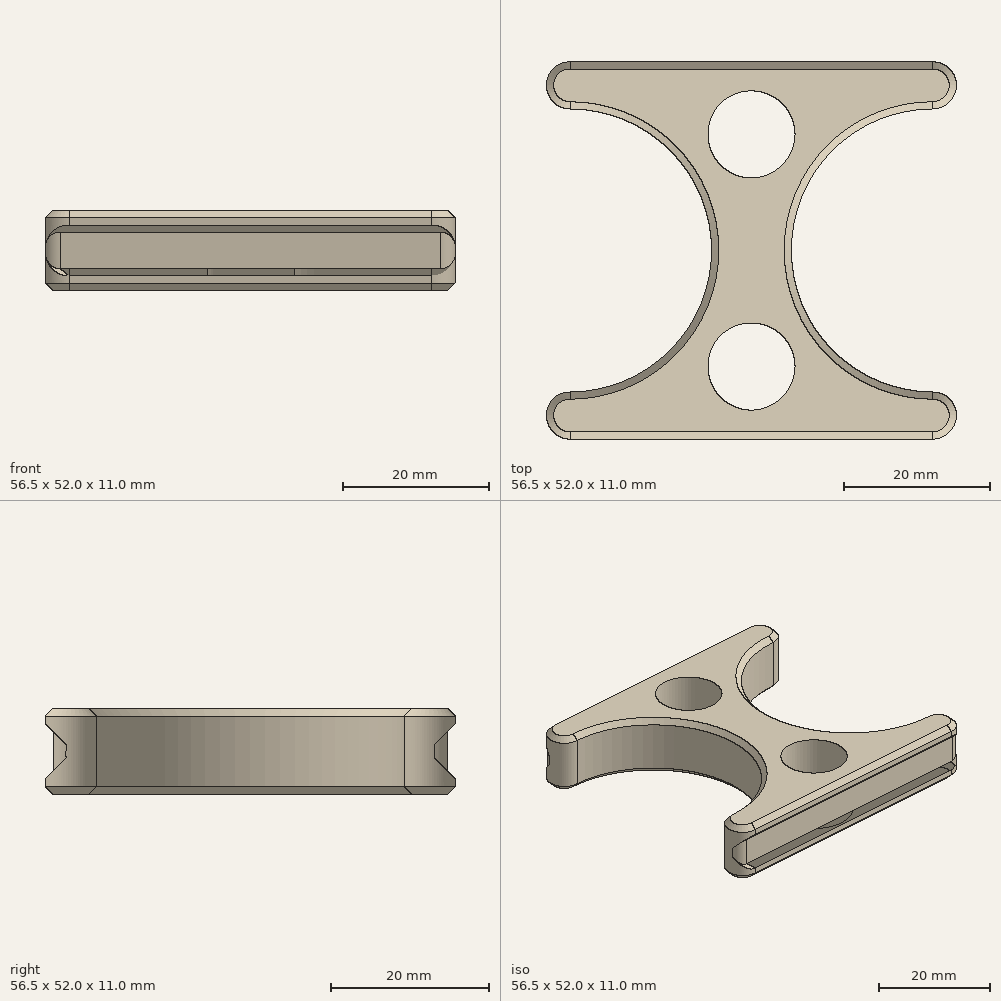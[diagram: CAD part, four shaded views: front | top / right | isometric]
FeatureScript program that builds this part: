
annotation { "Feature Type Name" : "Feature", "Feature Type Description" : "" }
export const myFeature = defineFeature(function(context is Context, id is Id, definition is map)
    precondition{}
    {
        {
            var Q0;
            Q0=qCreatedBy(makeId("Top.planeOp"),FACE);
            var sketch = newSketch(context, id + "F0", { "sketchPlane" : qUnion([Q0])});
            skLineSegment(sketch, "E0.rect.bottom", {"start": v(25, 26) * mm, "end": v(-25, 26) * mm, "construction": true});
            skLineSegment(sketch, "E0.rect.top", {"start": v(25, -26) * mm, "end": v(-25, -26) * mm, "construction": true});
            skLineSegment(sketch, "E0.rect.left", {"start": v(25, 26) * mm, "end": v(25, -26) * mm, "construction": true});
            skLineSegment(sketch, "E0.rect.right", {"start": v(-25, 26) * mm, "end": v(-25, -26) * mm, "construction": true});
            skPoint(sketch, "E0.rect.middle", {"position": v(0, 0) * mm});
            skLineSegment(sketch, "E1.rect.bottom", {"start": v(25, 19.5) * mm, "end": v(-25, 19.5) * mm, "construction": true});
            skLineSegment(sketch, "E1.rect.top", {"start": v(25, -19.5) * mm, "end": v(-25, -19.5) * mm, "construction": true});
            skLineSegment(sketch, "E1.rect.left", {"start": v(25, 19.5) * mm, "end": v(25, -19.5) * mm, "construction": true});
            skLineSegment(sketch, "E1.rect.right", {"start": v(-25, 19.5) * mm, "end": v(-25, -19.5) * mm, "construction": true});
            skArc(sketch, "E2", {"start": v(-25, -19.5) * mm, "mid": v(-5.5, 0) * mm, "end": v(-25, 19.5) * mm});
            skArc(sketch, "E3", {"start": v(25, 19.5) * mm, "mid": v(5.5, 0) * mm, "end": v(25, -19.5) * mm});
            skLineSegment(sketch, "E4", {"start": v(-25, -26) * mm, "end": v(25, -26) * mm});
            skLineSegment(sketch, "E5", {"start": v(-25, 26) * mm, "end": v(25, 26) * mm});
            skLineSegment(sketch, "E6", {"start": v(-25, 26) * mm, "end": v(-25, 19.5) * mm, "construction": true});
            skLineSegment(sketch, "E7", {"start": v(25, 26) * mm, "end": v(25, 19.5) * mm, "construction": true});
            skLineSegment(sketch, "E8", {"start": v(25, -19.5) * mm, "end": v(25, -26) * mm, "construction": true});
            skLineSegment(sketch, "E9", {"start": v(-25, -19.5) * mm, "end": v(-25, -26) * mm, "construction": true});
            skArc(sketch, "E10", {"start": v(-25, 26) * mm, "mid": v(-28.25, 22.75) * mm, "end": v(-25, 19.5) * mm});
            skArc(sketch, "E11", {"start": v(25, 19.5) * mm, "mid": v(28.25, 22.75) * mm, "end": v(25, 26) * mm});
            skArc(sketch, "E12", {"start": v(25, -26) * mm, "mid": v(28.25, -22.75) * mm, "end": v(25, -19.5) * mm});
            skArc(sketch, "E13", {"start": v(-25, -19.5) * mm, "mid": v(-28.25, -22.75) * mm, "end": v(-25, -26) * mm});
            skArc(sketch, "E14.0", {"start": v(-25, -21.5) * mm, "mid": v(-26.25, -22.75) * mm, "end": v(-25, -24) * mm});
            skLineSegment(sketch, "E14.1", {"start": v(-25, -24) * mm, "end": v(25, -24) * mm});
            skArc(sketch, "E14.2", {"start": v(-25, -21.5) * mm, "mid": v(-3.5, 0) * mm, "end": v(-25, 21.5) * mm});
            skArc(sketch, "E14.3", {"start": v(25, -24) * mm, "mid": v(26.25, -22.75) * mm, "end": v(25, -21.5) * mm});
            skArc(sketch, "E14.4", {"start": v(-25, 24) * mm, "mid": v(-26.25, 22.75) * mm, "end": v(-25, 21.5) * mm});
            skLineSegment(sketch, "E14.5", {"start": v(-25, 24) * mm, "end": v(25, 24) * mm});
            skArc(sketch, "E14.6", {"start": v(25, 21.5) * mm, "mid": v(26.25, 22.75) * mm, "end": v(25, 24) * mm});
            skArc(sketch, "E14.7", {"start": v(25, 21.5) * mm, "mid": v(3.5, 0) * mm, "end": v(25, -21.5) * mm});
            skSolve(sketch);
        }
        {
            var Q0;
            Q0=makeQuery(id+"F0.imprint","IMPRINT",FACE,{"disambiguationData":[TD([[makeQuery(id+"F0.imprint","IMPRINT",EDGE,{"derivedFrom":sQuery(id+"F0.wireOp",EDGE,"E2")}),-1.0]])]});
            var Q1;
            Q1=makeQuery(id+"F0.imprint","IMPRINT",FACE,{"disambiguationData":[TD([[makeQuery(id+"F0.imprint","IMPRINT",EDGE,{"derivedFrom":sQuery(id+"F0.wireOp",EDGE,"E14.0")}),1.0]])]});
            extrude(context, id + "F1", {"entities" : qUnion([Q0, Q1]), "depth" : 11 * mm});
        }
        {
            var Q0;
            Q0=makeQuery(id+"F1.opExtrude","SWEPT_FACE",FACE,{"disambiguationData":[OSD([sQuery(id+"F0.wireOp",EDGE,"E4")])]});
            var sketch = newSketch(context, id + "F2", { "sketchPlane" : qUnion([Q0])});
            skLineSegment(sketch, "E15", {"start": v(0, 11) * mm, "end": v(0, 0) * mm, "construction": true});
            skLineSegment(sketch, "E16.rect.bottom", {"start": v(34.25, 9) * mm, "end": v(-34.25, 9) * mm});
            skLineSegment(sketch, "E16.rect.top", {"start": v(34.25, 2) * mm, "end": v(-34.25, 2) * mm});
            skLineSegment(sketch, "E16.rect.left", {"start": v(34.25, 9) * mm, "end": v(34.25, 2) * mm});
            skLineSegment(sketch, "E16.rect.right", {"start": v(-34.25, 9) * mm, "end": v(-34.25, 2) * mm});
            skPoint(sketch, "E16.rect.middle", {"position": v(0, 5.5) * mm});
            skSolve(sketch);
        }
        {
            var Q0;
            {var subQ0=sQuery(id+"F2.wireOp",EDGE,"E16.rect.right");Q0=makeQuery(id+"F2.imprint","IMPRINT",FACE,{"disambiguationData":[TD([[makeQuery(id+"F2.imprint","IMPRINT",EDGE,{"derivedFrom":subQ0}),1.0]])]});}
            var Q1;
            {var subQ0=sQuery(id+"F2.wireOp",EDGE,"E16.rect.bottom");var subQ1=sQuery(id+"F0.wireOp",EDGE,"E4");var subQ2=makeQuery(id+"F1.opExtrude","SWEPT_EDGE",EDGE,{"disambiguationData":[OSD([subQ1,sQuery(id+"F0.wireOp",EDGE,"E12")])]});var subQ3=makeQuery(id+"F2.imprint","INTERSECT",VERTEX,{"derivedFrom":[subQ2,subQ0]});Q1=makeQuery(id+"F2.imprint","IMPRINT",FACE,{"disambiguationData":[TD([[makeQuery(id+"F2.imprint","IMPRINT",EDGE,{"disambiguationData":[TD([[subQ3,-1.0]])],"derivedFrom":subQ0}),1.0]])]});}
            var Q2;
            {var subQ0=sQuery(id+"F2.wireOp",EDGE,"E16.rect.left");Q2=makeQuery(id+"F2.imprint","IMPRINT",FACE,{"disambiguationData":[TD([[makeQuery(id+"F2.imprint","IMPRINT",EDGE,{"derivedFrom":subQ0}),-1.0]])]});}
            extrude(context, id + "F3", {"entities" : qUnion([Q0, Q1, Q2]), "oppositeDirection" : true, "depth" : 1 * mm});
        }
        {
            var Q0;
            Q0=makeQuery(id+"F3.opExtrude","SWEPT_BODY",BODY,{"disambiguationData":[OSD([sQuery(id+"F2.wireOp",EDGE,"E16.rect.bottom"),sQuery(id+"F2.wireOp",EDGE,"E16.rect.top"),sQuery(id+"F2.wireOp",EDGE,"E16.rect.left"),sQuery(id+"F2.wireOp",EDGE,"E16.rect.right")])]});
            transform(context, id + "F4", {"entities" : qUnion([Q0]), "transformType" : TransformType.TRANSLATION_3D, "dx" : 0 * mm, "dy" : 51 * mm, "dz" : 0 * mm, "makeCopy" : true});
        }
        {
            var Q0;
            Q0=makeQuery(id+"F4.opPattern","COPY",BODY,{"derivedFrom":makeQuery(id+"F3.opExtrude","SWEPT_BODY",BODY,{"disambiguationData":[OSD([sQuery(id+"F2.wireOp",EDGE,"E16.rect.bottom"),sQuery(id+"F2.wireOp",EDGE,"E16.rect.top"),sQuery(id+"F2.wireOp",EDGE,"E16.rect.left"),sQuery(id+"F2.wireOp",EDGE,"E16.rect.right")])]}),"instanceName":"1"});
            var Q1;
            Q1=makeQuery(id+"F3.opExtrude","SWEPT_BODY",BODY,{"disambiguationData":[OSD([sQuery(id+"F2.wireOp",EDGE,"E16.rect.bottom"),sQuery(id+"F2.wireOp",EDGE,"E16.rect.top"),sQuery(id+"F2.wireOp",EDGE,"E16.rect.left"),sQuery(id+"F2.wireOp",EDGE,"E16.rect.right")])]});
            var Q2;
            Q2=makeQuery(id+"F1.opExtrude","SWEPT_BODY",BODY,{"disambiguationData":[OSD([sQuery(id+"F0.wireOp",EDGE,"E2"),sQuery(id+"F0.wireOp",EDGE,"E3"),sQuery(id+"F0.wireOp",EDGE,"E4"),sQuery(id+"F0.wireOp",EDGE,"E5"),sQuery(id+"F0.wireOp",EDGE,"E10"),sQuery(id+"F0.wireOp",EDGE,"E11"),sQuery(id+"F0.wireOp",EDGE,"E12"),sQuery(id+"F0.wireOp",EDGE,"E13")])]});
            booleanBodies(context, id + "F5", {"operationType" : BooleanOperationType.SUBTRACTION, "tools" : qUnion([Q0, Q1]), "targets" : qUnion([Q2])});
        }
        {
            var Q0;
            Q0=makeQuery(id+"F1.opExtrude","CAP_EDGE",EDGE,{"disambiguationData":[OSD([sQuery(id+"F0.wireOp",EDGE,"E2")])],"isStart":false});
            var Q1;
            Q1=makeQuery(id+"F1.opExtrude","CAP_EDGE",EDGE,{"disambiguationData":[OSD([sQuery(id+"F0.wireOp",EDGE,"E2")])],"isStart":true});
            chamfer(context, id + "F6", {"entities" : qUnion([Q0, Q1]), "width" : 1 * mm, "tangentPropagation" : true});
        }
        {
            var Q0;
            Q0=makeQuery(id+"F5.opBoolean","COPY",EDGE,{"derivedFrom":makeQuery(id+"F3.opExtrude","CAP_EDGE",EDGE,{"disambiguationData":[OSD([sQuery(id+"F2.wireOp",EDGE,"E16.rect.bottom")])],"isStart":false})});
            var Q1;
            Q1=makeQuery(id+"F5.opBoolean","COPY",EDGE,{"derivedFrom":makeQuery(id+"F3.opExtrude","CAP_EDGE",EDGE,{"disambiguationData":[OSD([sQuery(id+"F2.wireOp",EDGE,"E16.rect.top")])],"isStart":false})});
            var Q2;
            Q2=makeQuery(id+"F5.opBoolean","COPY",EDGE,{"derivedFrom":makeQuery(id+"F4.opPattern","COPY",EDGE,{"derivedFrom":makeQuery(id+"F3.opExtrude","CAP_EDGE",EDGE,{"disambiguationData":[OSD([sQuery(id+"F2.wireOp",EDGE,"E16.rect.bottom")])],"isStart":true}),"instanceName":"1"})});
            var Q3;
            Q3=makeQuery(id+"F5.opBoolean","COPY",EDGE,{"derivedFrom":makeQuery(id+"F4.opPattern","COPY",EDGE,{"derivedFrom":makeQuery(id+"F3.opExtrude","CAP_EDGE",EDGE,{"disambiguationData":[OSD([sQuery(id+"F2.wireOp",EDGE,"E16.rect.top")])],"isStart":true}),"instanceName":"1"})});
            chamfer(context, id + "F7", {"entities" : qUnion([Q0, Q1, Q2, Q3]), "width" : 1 * mm});
        }
        {
            var Q0;
            Q0=makeQuery(id+"F5.opBoolean","INTERSECT",EDGE,{"derivedFrom":[makeQuery(id+"F1.opExtrude","SWEPT_FACE",FACE,{"disambiguationData":[OSD([sQuery(id+"F0.wireOp",EDGE,"E11")])]}),makeQuery(id+"F4.opPattern","COPY",FACE,{"derivedFrom":makeQuery(id+"F3.opExtrude","CAP_FACE",FACE,{"disambiguationData":[OSD([sQuery(id+"F2.wireOp",EDGE,"E16.rect.bottom"),sQuery(id+"F2.wireOp",EDGE,"E16.rect.top"),sQuery(id+"F2.wireOp",EDGE,"E16.rect.left"),sQuery(id+"F2.wireOp",EDGE,"E16.rect.right")])],"isStart":true}),"instanceName":"1"})]});
            var Q1;
            Q1=makeQuery(id+"F5.opBoolean","INTERSECT",EDGE,{"derivedFrom":[makeQuery(id+"F1.opExtrude","SWEPT_FACE",FACE,{"disambiguationData":[OSD([sQuery(id+"F0.wireOp",EDGE,"E10")])]}),makeQuery(id+"F4.opPattern","COPY",FACE,{"derivedFrom":makeQuery(id+"F3.opExtrude","CAP_FACE",FACE,{"disambiguationData":[OSD([sQuery(id+"F2.wireOp",EDGE,"E16.rect.bottom"),sQuery(id+"F2.wireOp",EDGE,"E16.rect.top"),sQuery(id+"F2.wireOp",EDGE,"E16.rect.left"),sQuery(id+"F2.wireOp",EDGE,"E16.rect.right")])],"isStart":true}),"instanceName":"1"})]});
            var Q2;
            Q2=makeQuery(id+"F5.opBoolean","INTERSECT",EDGE,{"derivedFrom":[makeQuery(id+"F1.opExtrude","SWEPT_FACE",FACE,{"disambiguationData":[OSD([sQuery(id+"F0.wireOp",EDGE,"E13")])]}),makeQuery(id+"F3.opExtrude","CAP_FACE",FACE,{"disambiguationData":[OSD([sQuery(id+"F2.wireOp",EDGE,"E16.rect.bottom"),sQuery(id+"F2.wireOp",EDGE,"E16.rect.top"),sQuery(id+"F2.wireOp",EDGE,"E16.rect.left"),sQuery(id+"F2.wireOp",EDGE,"E16.rect.right")])],"isStart":false})]});
            var Q3;
            Q3=makeQuery(id+"F5.opBoolean","INTERSECT",EDGE,{"derivedFrom":[makeQuery(id+"F1.opExtrude","SWEPT_FACE",FACE,{"disambiguationData":[OSD([sQuery(id+"F0.wireOp",EDGE,"E12")])]}),makeQuery(id+"F3.opExtrude","CAP_FACE",FACE,{"disambiguationData":[OSD([sQuery(id+"F2.wireOp",EDGE,"E16.rect.bottom"),sQuery(id+"F2.wireOp",EDGE,"E16.rect.top"),sQuery(id+"F2.wireOp",EDGE,"E16.rect.left"),sQuery(id+"F2.wireOp",EDGE,"E16.rect.right")])],"isStart":false})]});
            fillet(context, id + "F8", {"entities" : qUnion([Q0, Q1, Q2, Q3]), "radius" : 2 * mm, "allowEdgeOverflow" : false});
        }
        {
            var Q0;
            Q0=makeQuery(id+"F1.opExtrude","CAP_FACE",FACE,{"disambiguationData":[OSD([sQuery(id+"F0.wireOp",EDGE,"E2"),sQuery(id+"F0.wireOp",EDGE,"E3"),sQuery(id+"F0.wireOp",EDGE,"E4"),sQuery(id+"F0.wireOp",EDGE,"E5"),sQuery(id+"F0.wireOp",EDGE,"E10"),sQuery(id+"F0.wireOp",EDGE,"E11"),sQuery(id+"F0.wireOp",EDGE,"E12"),sQuery(id+"F0.wireOp",EDGE,"E13")])],"isStart":false});
            var sketch = newSketch(context, id + "F9", { "sketchPlane" : qUnion([Q0])});
            skCircle(sketch, "E17", {"center": v(0, -16) * mm, "radius": 6 * mm});
            skPoint(sketch, "E17.centerSnap0", {"position": v(0, -25) * mm});
            skCircle(sketch, "E18.MirrorC", {"center": v(0, 16) * mm, "radius": 6 * mm});
            skSolve(sketch);
        }
        {
            var Q0;
            Q0 = qSketchRegion(id + "F9", true);
            extrude(context, id + "F10", {"entities" : qUnion([Q0]), "operationType" : NewBodyOperationType.REMOVE, "endBound" : BoundingType.THROUGH_ALL, "oppositeDirection" : true, "depth" : 25 * mm});
        }
        {
            var Q0;
            Q0=makeQuery(id+"F10.boolean.opBoolean","COPY",EDGE,{"derivedFrom":makeQuery(id+"F10.opExtrude","CAP_EDGE",EDGE,{"disambiguationData":[OSD([sQuery(id+"F9.wireOp",EDGE,"E18.MirrorC")])],"isStart":true})});
            var Q1;
            Q1=makeQuery(id+"F10.boolean.opBoolean","COPY",EDGE,{"derivedFrom":makeQuery(id+"F10.opExtrude","CAP_EDGE",EDGE,{"disambiguationData":[OSD([sQuery(id+"F9.wireOp",EDGE,"E17")])],"isStart":true})});
            var Q2;
            Q2=makeQuery(id+"F10.boolean.opBoolean","INTERSECT",EDGE,{"derivedFrom":[makeQuery(id+"F1.opExtrude","CAP_FACE",FACE,{"disambiguationData":[OSD([sQuery(id+"F0.wireOp",EDGE,"E2"),sQuery(id+"F0.wireOp",EDGE,"E3"),sQuery(id+"F0.wireOp",EDGE,"E4"),sQuery(id+"F0.wireOp",EDGE,"E5"),sQuery(id+"F0.wireOp",EDGE,"E10"),sQuery(id+"F0.wireOp",EDGE,"E11"),sQuery(id+"F0.wireOp",EDGE,"E12"),sQuery(id+"F0.wireOp",EDGE,"E13")])],"isStart":true}),makeQuery(id+"F10.opExtrude","SWEPT_FACE",FACE,{"disambiguationData":[OSD([sQuery(id+"F9.wireOp",EDGE,"E17")])]})]});
            var Q3;
            Q3=makeQuery(id+"F10.boolean.opBoolean","INTERSECT",EDGE,{"derivedFrom":[makeQuery(id+"F1.opExtrude","CAP_FACE",FACE,{"disambiguationData":[OSD([sQuery(id+"F0.wireOp",EDGE,"E2"),sQuery(id+"F0.wireOp",EDGE,"E3"),sQuery(id+"F0.wireOp",EDGE,"E4"),sQuery(id+"F0.wireOp",EDGE,"E5"),sQuery(id+"F0.wireOp",EDGE,"E10"),sQuery(id+"F0.wireOp",EDGE,"E11"),sQuery(id+"F0.wireOp",EDGE,"E12"),sQuery(id+"F0.wireOp",EDGE,"E13")])],"isStart":true}),makeQuery(id+"F10.opExtrude","SWEPT_FACE",FACE,{"disambiguationData":[OSD([sQuery(id+"F9.wireOp",EDGE,"E18.MirrorC")])]})]});
            chamfer(context, id + "F11", {"entities" : qUnion([Q0, Q1, Q2, Q3]), "width" : 1 * mm, "tangentPropagation" : true});
        }
    });
